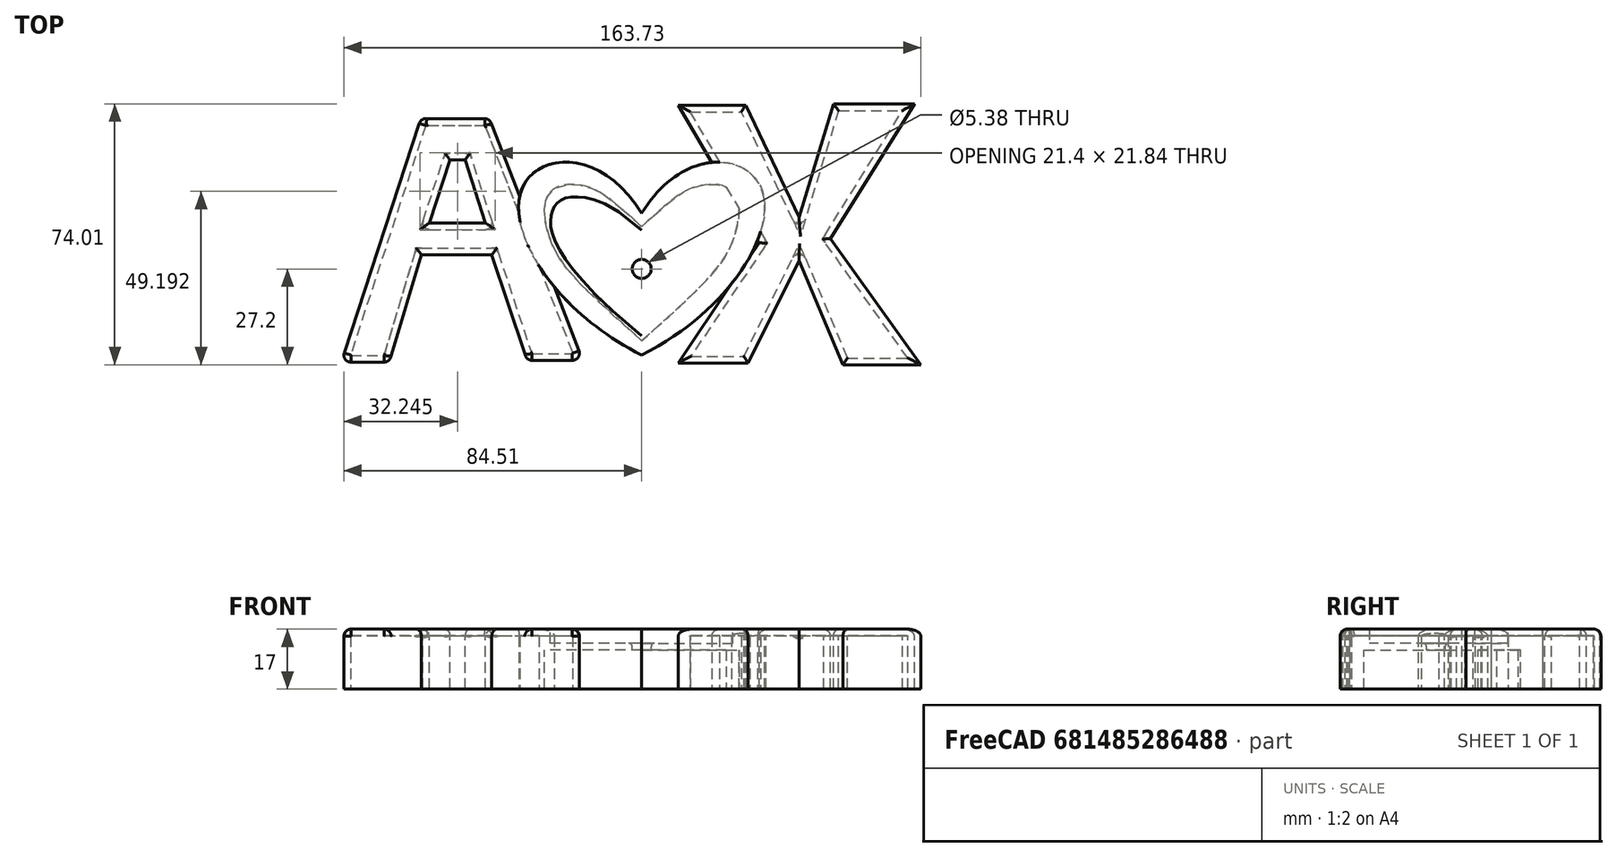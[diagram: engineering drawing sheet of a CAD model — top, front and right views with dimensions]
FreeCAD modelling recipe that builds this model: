
FCSTD DOCUMENT  (FreeCAD 0.19R24267 +148 (Git))
Label: alovex
License: All rights reserved
LicenseURL: http://en.wikipedia.org/wiki/All_rights_reserved
objects: PartDesign::Fillet×14, Sketcher::SketchObject×7, PartDesign::Pocket×4, App::MeasureDistance×4, PartDesign::Pad×3, PartDesign::Body×3, PartDesign::Thickness×2, Part::MultiFuse×1, Mesh::Feature×1
note: 57 computed .brp shape members not serialized (recipe doc carries the construction recipe); baked Part::Feature solids carry a one-line shape summary decoded from their .brp

FEATURE [Sketcher::SketchObject] Sketch
  FullyConstrained = false
  MapMode = 5
  Support = -> [XY_Plane]
  sketch-geometry (6):
    g0: Circle CenterX=0 CenterY=18.5619 CenterZ=0 NormalX=0 NormalY=0 NormalZ=1 AngleXU=0 Radius=1
    g1: Circle CenterX=0 CenterY=-21.6834 CenterZ=0 NormalX=0 NormalY=0 NormalZ=1 AngleXU=0 Radius=1
    g2: BSplineCurve PolesCount=5 KnotsCount=3 Degree=3 IsPeriodic=0
    g3: GeomPoint X=0 Y=18.5619 Z=0
    g4: GeomPoint X=0 Y=-21.6834 Z=0
    g5: BSplineCurve PolesCount=5 KnotsCount=3 Degree=3 IsPeriodic=0
  constraints (8):
    c: PointOnObject(g2,g-2)
    c: Weight(g0) = 1
    c: Equal(g0,g1)
    c: PointOnObject(g2,g-2)
    c: InternalAlignment(g0,g2)
    c: InternalAlignment(g1,g2)
    c: InternalAlignment(g3,g2)
    c: InternalAlignment(g4,g2)
FEATURE [Sketcher::SketchObject] Sketch001
  FullyConstrained = false
  MapMode = 5
  Support = -> [XY_Plane001]
  sketch-geometry (12):
    g0: LineSegment StartX=10.3658 StartY=49.2566 StartZ=0 EndX=33.3169 EndY=10.1732 EndZ=0
    g1: LineSegment StartX=33.3169 StartY=10.1732 StartZ=0 EndX=10.3658 EndY=-23.9209 EndZ=0
    g2: LineSegment StartX=30.157 StartY=-23.9209 StartZ=0 EndX=44.6262 EndY=5.18378 EndZ=0
    g3: LineSegment StartX=44.6262 StartY=5.18378 StartZ=0 EndX=57.0996 EndY=-24.4199 EndZ=0
    g4: LineSegment StartX=79.2192 StartY=-24.4199 StartZ=0 EndX=53.6071 EndY=11.3374 EndZ=0
    g5: LineSegment StartX=53.6071 StartY=11.3374 StartZ=0 EndX=77.3898 EndY=49.5892 EndZ=0
    g6: LineSegment StartX=54.4386 StartY=49.5892 StartZ=0 EndX=44.6262 EndY=17.4909 EndZ=0
    g7: LineSegment StartX=44.6262 StartY=17.4909 StartZ=0 EndX=29.4917 EndY=49.2566 EndZ=0
    g8: LineSegment StartX=10.3658 StartY=49.2566 StartZ=0 EndX=29.4917 EndY=49.2566 EndZ=0
    g9: LineSegment StartX=54.4386 StartY=49.5892 StartZ=0 EndX=77.3898 EndY=49.5892 EndZ=0
    g10: LineSegment StartX=57.0996 StartY=-24.4199 StartZ=0 EndX=79.2192 EndY=-24.4199 EndZ=0
    g11: LineSegment StartX=10.3658 StartY=-23.9209 StartZ=0 EndX=30.157 EndY=-23.9209 EndZ=0
  constraints (16):
    c: Coincident(g1,g0)
    c: Coincident(g3,g2)
    c: Coincident(g5,g4)
    c: Coincident(g7,g6)
    c: Coincident(g8,g0)
    c: Coincident(g8,g7)
    c: Horizontal(g8)
    c: Coincident(g9,g6)
    c: Coincident(g9,g5)
    c: Horizontal(g9)
    c: Coincident(g10,g3)
    c: Coincident(g10,g4)
    c: Horizontal(g10)
    c: Coincident(g11,g1)
    c: Coincident(g11,g2)
    c: Horizontal(g11)
FEATURE [PartDesign::Pad] Pad
  Direction = (1,1,1)
  Length = 17
  Length2 = 100
  Profile = -> Sketch
  Type = 0
FEATURE [PartDesign::Pad] Pad002
  Direction = (1,1,1)
  Length = 17
  Length2 = 100
  Profile = -> Sketch001
  Type = 0
FEATURE [Sketcher::SketchObject] Sketch003
  FullyConstrained = false
  MapMode = 5
  Support = -> [XY_Plane]
  sketch-geometry (12):
    g0-g5: Circle x6 (B-spline internal-alignment scaffolding for g6; pole/knot coordinates omitted)
    g6: BSplineCurve PolesCount=6 KnotsCount=4 Degree=3 IsPeriodic=0
    g7-g10: GeomPoint x4 (B-spline internal-alignment scaffolding for g6; pole/knot coordinates omitted)
    g11: BSplineCurve PolesCount=6 KnotsCount=4 Degree=3 IsPeriodic=0
  constraints (4):
    c: PointOnObject(g6,g-2)
    c: PointOnObject(g6,g-2)
    c: InternalAlignment(g0-g5 -> g6) x6
    c: InternalAlignment(g7-g10 -> g6) x4
FEATURE [PartDesign::Pocket] Pocket
  BaseFeature = -> Pad
  Length = 2
  Length2 = 100
  Offset = 6
  Profile = -> Sketch003
  Type = 3
  UpToFace = -> Pad [Face4]
  expr: Length = 2mm
FEATURE [App::MeasureDistance] Distance  label="Distance: 17.00 mm"
  Distance = 17
  P1 = (0,-21.6834,17)
  P2 = (0,-21.6834,0)
FEATURE [App::MeasureDistance] Distance001  label="Distance: 10.94 mm"
  Distance = 10.9405
  P1 = (0,14.7515,10.9405)
  P2 = (0,14.7515,0)
FEATURE [Sketcher::SketchObject] Sketch004
  FullyConstrained = false
  MapMode = 5
  Placement = pos=(0,0,17) rot=(0,0,1;0rad)
  Support = -> [Pocket]
  sketch-geometry (12):
    g0-g5: Circle x6 (B-spline internal-alignment scaffolding for g6; pole/knot coordinates omitted)
    g6: BSplineCurve PolesCount=6 KnotsCount=4 Degree=3 IsPeriodic=0
    g7-g10: GeomPoint x4 (B-spline internal-alignment scaffolding for g6; pole/knot coordinates omitted)
    g11: BSplineCurve PolesCount=6 KnotsCount=4 Degree=3 IsPeriodic=0
  constraints (4):
    c: PointOnObject(g6,g-2)
    c: PointOnObject(g6,g-2)
    c: InternalAlignment(g0-g5 -> g6) x6
    c: InternalAlignment(g7-g10 -> g6) x4
FEATURE [PartDesign::Pocket] Pocket001
  BaseFeature = -> Pocket
  Length = 4
  Length2 = 100
  Profile = -> Sketch004
  Type = 0
FEATURE [Sketcher::SketchObject] Sketch005
  FullyConstrained = false
  MapMode = 5
  Placement = pos=(0,0,13) rot=(0,0,1;0rad)
  Support = -> [Pocket001]
  sketch-geometry (1):
    g0: Circle CenterX=0 CenterY=2.78007 CenterZ=0 NormalX=0 NormalY=0 NormalZ=1 AngleXU=0 Radius=2.6896
  constraints (1):
    c: PointOnObject(g0,g-2)
FEATURE [PartDesign::Pocket] Pocket002
  BaseFeature = -> Pocket001
  Length = 2
  Length2 = 100
  Profile = -> Sketch005
  Type = 0
FEATURE [Sketcher::SketchObject] Sketch002
  FullyConstrained = false
  MapMode = 5
  Support = -> [XY_Plane002]
  sketch-geometry (8):
    g0: LineSegment StartX=-62.6455 StartY=45.4314 StartZ=0 EndX=-85.2729 EndY=-23.6735 EndZ=0
    g1: LineSegment StartX=-43.1869 StartY=45.4314 StartZ=0 EndX=-16.7542 EndY=-23.1703 EndZ=0
    g2: LineSegment StartX=-85.2729 StartY=-23.6735 StartZ=0 EndX=-71.6374 EndY=-23.6735 EndZ=0
    g3: LineSegment StartX=-71.6374 StartY=-23.6735 StartZ=0 EndX=-62.4902 EndY=6.76595 EndZ=0
    g4: LineSegment StartX=-62.4902 StartY=6.76595 StartZ=0 EndX=-42.5327 EndY=6.76595 EndZ=0
    g5: LineSegment StartX=-42.5327 StartY=6.76595 StartZ=0 EndX=-32.5539 EndY=-23.1703 EndZ=0
    g6: LineSegment StartX=-32.5539 StartY=-23.1703 StartZ=0 EndX=-16.7542 EndY=-23.1703 EndZ=0
    g7: LineSegment StartX=-62.6455 StartY=45.4314 StartZ=0 EndX=-43.1869 EndY=45.4314 EndZ=0
  constraints (12):
    c: Coincident(g2,g0)
    c: Horizontal(g2)
    c: Coincident(g3,g2)
    c: Coincident(g4,g3)
    c: Horizontal(g4)
    c: Coincident(g5,g4)
    c: Coincident(g6,g5)
    c: Coincident(g6,g1)
    c: Horizontal(g6)
    c: Coincident(g7,g0)
    c: Coincident(g7,g1)
    c: Horizontal(g7)
FEATURE [PartDesign::Pad] Pad001
  Direction = (1,1,1)
  Length = 17
  Length2 = 100
  Profile = -> Sketch002
  Type = 0
FEATURE [Sketcher::SketchObject] Sketch006
  FullyConstrained = false
  MapMode = 5
  Placement = pos=(0,0,0) rot=(1,0,0;3.14159rad)
  Support = -> [Pad001]
  sketch-geometry (4):
    g0: LineSegment StartX=-60.2087 StartY=-15.8532 StartZ=0 EndX=-44.3205 EndY=-15.8532 EndZ=0
    g1: LineSegment StartX=-44.3205 StartY=-15.8532 StartZ=0 EndX=-50.1236 EndY=-33.6905 EndZ=0
    g2: LineSegment StartX=-50.1236 StartY=-33.6905 StartZ=0 EndX=-54.4057 EndY=-33.6905 EndZ=0
    g3: LineSegment StartX=-60.2087 StartY=-15.8532 StartZ=0 EndX=-54.4057 EndY=-33.6905 EndZ=0
  constraints (7):
    c: Horizontal(g0)
    c: Coincident(g0,g1)
    c: Coincident(g1,g2)
    c: Horizontal(g2)
    c: Coincident(g3,g0)
    c: Coincident(g3,g2)
    c: Equal(g3,g1)
FEATURE [PartDesign::Pocket] Pocket003
  BaseFeature = -> Pad001
  Length = 0
  Length2 = 100
  Offset = 8
  Profile = -> Sketch006
  Type = 3
  UpToFace = -> Pad001 [Face10]
FEATURE [PartDesign::Fillet] Fillet
  Base = -> Pocket003 [Edge10]
  BaseFeature = -> Pocket003
  Radius = 2
  SupportTransform = false
FEATURE [PartDesign::Fillet] Fillet001
  Base = -> Fillet [Edge4]
  BaseFeature = -> Fillet
  Radius = 2
  SupportTransform = false
FEATURE [PartDesign::Fillet] Fillet002
  Base = -> Fillet001 [Edge43]
  BaseFeature = -> Fillet001
  Radius = 2
  SupportTransform = false
FEATURE [PartDesign::Fillet] Fillet003
  Base = -> Fillet002 [Edge28]
  BaseFeature = -> Fillet002
  Radius = 2
  SupportTransform = false
FEATURE [PartDesign::Fillet] Fillet004
  Base = -> Fillet003 [Edge31]
  BaseFeature = -> Fillet003
  Radius = 2
  SupportTransform = false
FEATURE [PartDesign::Fillet] Fillet005
  Base = -> Fillet004 [Edge42]
  BaseFeature = -> Fillet004
  Radius = 2
  SupportTransform = false
FEATURE [PartDesign::Fillet] Fillet006
  Base = -> Fillet005 [Edge2]
  BaseFeature = -> Fillet005
  Radius = 2
  SupportTransform = false
FEATURE [PartDesign::Fillet] Fillet007
  Base = -> Fillet006 [Edge20]
  BaseFeature = -> Fillet006
  Radius = 2
  SupportTransform = false
FEATURE [PartDesign::Fillet] Fillet008
  Base = -> Fillet007 [Edge8]
  BaseFeature = -> Fillet007
  Radius = 2
  SupportTransform = false
FEATURE [PartDesign::Fillet] Fillet009
  Base = -> Fillet008 [Edge4]
  BaseFeature = -> Fillet008
  Radius = 2
  SupportTransform = false
FEATURE [PartDesign::Fillet] Fillet010
  Base = -> Fillet009 [Edge17]
  BaseFeature = -> Fillet009
  Radius = 2
  SupportTransform = false
FEATURE [PartDesign::Fillet] Fillet011
  Base = -> Fillet010 [Edge15]
  BaseFeature = -> Fillet010
  Radius = 2
  SupportTransform = false
FEATURE [PartDesign::Fillet] Fillet012
  Base = -> Pad002 [Edge34,Face14,Edge31,Edge28,Edge25,Edge22,Edge19,Edge16,Edge13,Edge10,Edge7,Edge4,Edge36]
  BaseFeature = -> Pad002
  Radius = 2
  SupportTransform = false
FEATURE [PartDesign::Fillet] Fillet013
  Base = -> Pocket002 [Edge20]
  BaseFeature = -> Pocket002
  Radius = 1
  SupportTransform = false
FEATURE [PartDesign::Body] Body
  Group = -> [Sketch,Pad,Sketch003,Pocket,Sketch004,Pocket001,Sketch005,Pocket002,Fillet013]
  Origin = -> Origin
  Tip = -> Fillet013
FEATURE [PartDesign::Thickness] Thickness
  Base = -> Fillet012 [Face4]
  BaseFeature = -> Fillet012
  Intersection = false
  Join = 0
  Mode = 0
  Reversed = true
  SupportTransform = false
  Value = 1.9
FEATURE [PartDesign::Body] Body001
  Group = -> [Sketch001,Pad002,Fillet012,Thickness]
  Origin = -> Origin001
  Tip = -> Thickness
FEATURE [PartDesign::Thickness] Thickness001
  Base = -> Fillet011 [Face44]
  BaseFeature = -> Fillet011
  Intersection = false
  Join = 0
  Mode = 0
  Reversed = true
  SupportTransform = false
  Value = 1.9
FEATURE [PartDesign::Body] Body002
  Group = -> [Sketch002,Pad001,Sketch006,Pocket003,Fillet,Fillet001,Fillet002,Fillet003,Fillet004,Fillet005,Fillet006,Fillet007,Fillet008,Fillet009,Fillet010,Fillet011,Thickness001]
  Origin = -> Origin002
  Tip = -> Thickness001
FEATURE [Part::MultiFuse] Fusion
  Shapes = -> [Body002,Body001,Body]
FEATURE [App::MeasureDistance] Distance002  label="Distance: 163.73 mm"
  Distance = 163.726
  P1 = (-84.4887,-21.9877,15)
  P2 = (79.2192,-24.4199,15)
FEATURE [App::MeasureDistance] Distance003  label="Distance: 73.49 mm"
  Distance = 73.488
  P1 = (78.3629,-23.9799,16.2515)
  P2 = (77.2226,49.4963,15.6025)
FEATURE [Mesh::Feature] Mesh  label="Fusion (Meshed)"
